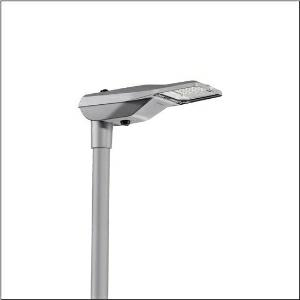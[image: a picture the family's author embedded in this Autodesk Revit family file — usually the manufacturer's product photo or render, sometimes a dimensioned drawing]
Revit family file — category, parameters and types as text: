
# Revit family: streetlight_sl_21_micro___st1_0ab_5xe1m33t08db_25ba
name_source: partatom
category: Lighting Fixtures
units: mm (PartAtom-declared; Revit-internal decimal feet)

## family parameters
Cut with Voids When Loaded = No
Host = Face
Light Source = No
Part Type = Normal
Room Calculation Point = No
Round Connector Dimension = Use Diameter
Shared = No

## types (1)
- --- (1 x LED, 4500 lm, 39.1 W, 3000K)
    Apparent Load = 39 VA
    CIE Flux Codes = 38 73 97 100 100
    Color Rendering = 70
    Color Temperature = 3000K
    Default Elevation = 1800 mm
    Description = Streetlight SL 21 micro, mast luminaire, primary light control with lens, of PMMA, primary optical cover: cover, of toughened safety glass, transparent, light distribution: ST1.0aB, light emission: direct distribution, primary light characteristic: asymmetric, installation type: side-entry, post-top, LED, High Power LED, rated luminous flux: 4.500lm, luminous efficacy: 115lm/W, light colour: 730, colour temperature: 3000K, control gear: D4i, control: flexible luminous flux parameterisation, time-dependent luminous flux control, constant luminous flux control, overheat protection, pre-setting: logarithmic dimming characteristic, mains connection: 220..240V, AC, 50/60Hz, start of lifetime: 39W, end of service life: 41W, reduction: 18W, luminaire housing, of diecast aluminium, powder-coated, SITECO metallic grey (DB 702S), corrosivity category C5 high according to DIN EN ISO 12944, please order mast flange separately, inclination adjustable: 0°, 5°, 10°, 15°, sealing non-destructively replaceable, multi-level sealing system, length: 528mm, width: 235mm, height: 110mm, mast flange for spigot size: 42mm (side-entry): 5XC10008XM4, 60/48mm (side-entry/post-top): 5XC10108XM2, 76/60mm (side-entry/post-top): 5XC10108XM1, Smart Interface below and above, protection rating (complete): IP66, insulation class (complete): insulation class II (safety insulation), certification: CE, ENEC, ENEC+, VDE, impact resistance: IK10, permissible operating ambient temperature for outdoor applications: -40..+50°C, standard-compliant lighting for roads and squares, packaging unit: 1 piece

Light Distribution: ST1.0aB
    Height = 110 mm
    Lamp = 1 x LED
    Lamp Light Flux = 4500 lm
    Lamp Power = 39.1 W
    Lamp count = 1
    Length = 528 mm
    Luminous efficacy = 115 lm/W
    Manufacturer = Siteco
    ModVariant = No
    Model = 5XE1M33T08DB
    Number of Poles = 1
    OnlyDefault = Yes
    Power Factor = 1
    Product Name = Streetlight SL 21 micro | ST1.0aB
    Product group = mast luminaire | pylon top
    ProductGroupID = 6100
    Protection Class = Protection class II
    Protection Degree = IP 66
    RLX_Detail_Level = 1
    RLX_Emergency_Light_Flux = 0 lm
    RLX_Emergency_Type = 0
    RLX_Emergency_Type_DB = No
    RlxData = <blob elided: 98317 chars, md5=6b7e01f4>
    Socket = socket
    Standby Power = 0 W
    System Light Flux = 4500 lm
    System Power = 39 W
    Type Comments = factory setting: luminous flux: 100 % | dim-lin: 254 | 765 mA
    Type Image = l_1007239.jpg
    URL = http://relux.com
    VarID = @adj_153431
    Voltage = 0 V
    Weight = 0.00 kg
    Width = 235 mm

## geometry (parser evidence)
native form markers: Blend x4, Sweep x10
no freeform markers — native parametric forms only
